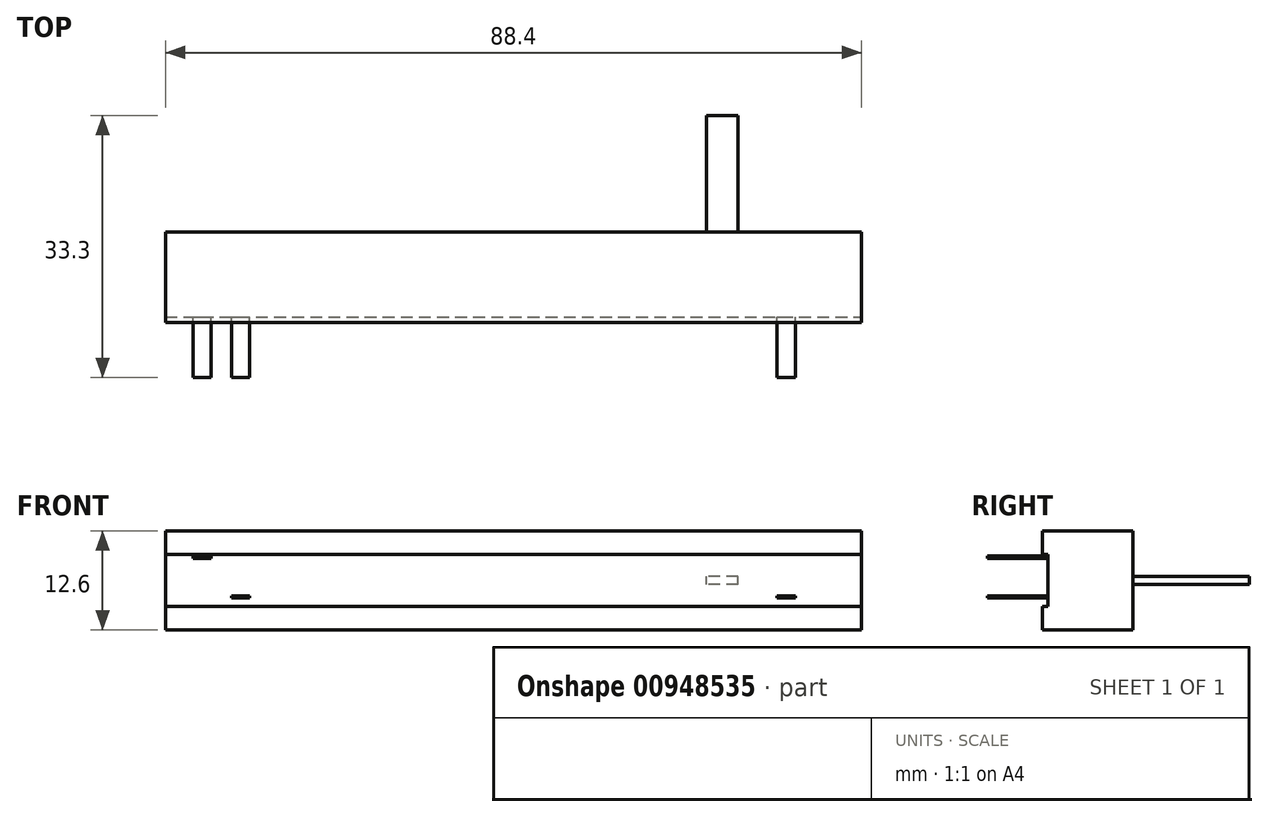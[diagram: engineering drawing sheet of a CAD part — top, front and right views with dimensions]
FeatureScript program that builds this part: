
annotation { "Feature Type Name" : "Feature", "Feature Type Description" : "" }
export const myFeature = defineFeature(function(context is Context, id is Id, definition is map)
    precondition{}
    {
        {
            var Q0;
            Q0=qCreatedBy(makeId("Front.planeOp"),FACE);
            var sketch = newSketch(context, id + "F0", { "sketchPlane" : qUnion([Q0])});
            skLineSegment(sketch, "E0.bottom", {"start": v(44.2, 6.3) * mm, "end": v(-44.2, 6.3) * mm});
            skLineSegment(sketch, "E0.top", {"start": v(44.2, -6.3) * mm, "end": v(-44.2, -6.3) * mm});
            skLineSegment(sketch, "E0.left", {"start": v(44.2, 6.3) * mm, "end": v(44.2, -6.3) * mm});
            skLineSegment(sketch, "E0.right", {"start": v(-44.2, 6.3) * mm, "end": v(-44.2, -6.3) * mm});
            skPoint(sketch, "E0.middle", {"position": v(0, 0) * mm});
            skLineSegment(sketch, "E1.bottom", {"start": v(-40.7, 2.82) * mm, "end": v(-38.4, 2.82) * mm});
            skLineSegment(sketch, "E1.top", {"start": v(-40.7, 3.1) * mm, "end": v(-38.4, 3.1) * mm});
            skLineSegment(sketch, "E1.left", {"start": v(-40.7, 2.82) * mm, "end": v(-40.7, 3.1) * mm});
            skLineSegment(sketch, "E1.right", {"start": v(-38.4, 2.82) * mm, "end": v(-38.4, 3.1) * mm});
            skLineSegment(sketch, "E2.bottom", {"start": v(-35.8, -1.92) * mm, "end": v(-33.5, -1.92) * mm});
            skLineSegment(sketch, "E2.top", {"start": v(-35.8, -2.2) * mm, "end": v(-33.5, -2.2) * mm});
            skLineSegment(sketch, "E2.left", {"start": v(-35.8, -1.92) * mm, "end": v(-35.8, -2.2) * mm});
            skLineSegment(sketch, "E2.right", {"start": v(-33.5, -1.92) * mm, "end": v(-33.5, -2.2) * mm});
            skLineSegment(sketch, "E3.bottom", {"start": v(33.5, -1.92) * mm, "end": v(35.8, -1.92) * mm});
            skLineSegment(sketch, "E3.top", {"start": v(33.5, -2.2) * mm, "end": v(35.8, -2.2) * mm});
            skLineSegment(sketch, "E3.left", {"start": v(33.5, -1.92) * mm, "end": v(33.5, -2.2) * mm});
            skLineSegment(sketch, "E3.right", {"start": v(35.8, -1.92) * mm, "end": v(35.8, -2.2) * mm});
            skLineSegment(sketch, "E4.bottom", {"start": v(-44.2, -6.3) * mm, "end": v(44.2, -6.3) * mm});
            skLineSegment(sketch, "E4.top", {"start": v(-44.2, -3.3) * mm, "end": v(44.2, -3.3) * mm});
            skLineSegment(sketch, "E4.left", {"start": v(-44.2, -6.3) * mm, "end": v(-44.2, -3.3) * mm});
            skLineSegment(sketch, "E4.right", {"start": v(44.2, -6.3) * mm, "end": v(44.2, -3.3) * mm});
            skLineSegment(sketch, "E5.bottom", {"start": v(-44.2, 6.3) * mm, "end": v(44.2, 6.3) * mm});
            skLineSegment(sketch, "E5.top", {"start": v(-44.2, 3.3) * mm, "end": v(44.2, 3.3) * mm});
            skLineSegment(sketch, "E5.left", {"start": v(-44.2, 6.3) * mm, "end": v(-44.2, 3.3) * mm});
            skLineSegment(sketch, "E5.right", {"start": v(44.2, 6.3) * mm, "end": v(44.2, 3.3) * mm});
            skSolve(sketch);
        }
        {
            var Q0;
            Q0=makeQuery(id+"F0.imprint","IMPRINT",FACE,{"disambiguationData":[TD([[makeQuery(id+"F0.imprint","IMPRINT",EDGE,{"derivedFrom":sQuery(id+"F0.wireOp",EDGE,"E0.bottom")}),1.0]])]});
            var Q1;
            Q1=makeQuery(id+"F0.imprint","IMPRINT",FACE,{"disambiguationData":[TD([[makeQuery(id+"F0.imprint","IMPRINT",EDGE,{"derivedFrom":sQuery(id+"F0.wireOp",EDGE,"E1.bottom")}),1.0]])]});
            var Q2;
            Q2=makeQuery(id+"F0.imprint","IMPRINT",FACE,{"disambiguationData":[TD([[makeQuery(id+"F0.imprint","IMPRINT",EDGE,{"derivedFrom":sQuery(id+"F0.wireOp",EDGE,"E2.bottom")}),-1.0]])]});
            var Q3;
            Q3=makeQuery(id+"F0.imprint","IMPRINT",FACE,{"disambiguationData":[TD([[makeQuery(id+"F0.imprint","IMPRINT",EDGE,{"derivedFrom":sQuery(id+"F0.wireOp",EDGE,"E3.bottom")}),-1.0]])]});
            var Q4;
            Q4=makeQuery(id+"F0.imprint","IMPRINT",FACE,{"disambiguationData":[TD([[makeQuery(id+"F0.imprint","IMPRINT",EDGE,{"derivedFrom":sQuery(id+"F0.wireOp",EDGE,"E1.bottom")}),-1.0]])]});
            var Q5;
            {var subQ0=sQuery(id+"F0.wireOp",EDGE,"E0.top");Q5=makeQuery(id+"F0.imprint","IMPRINT",FACE,{"disambiguationData":[TD([[makeQuery(id+"F0.imprint","IMPRINT",EDGE,{"derivedFrom":subQ0}),-1.0]])]});}
            extrude(context, id + "F1", {"entities" : qUnion([Q0, Q1, Q2, Q3, Q4, Q5]), "oppositeDirection" : true, "depth" : 10.8 * mm, "offsetDistance" : 25 * mm});
        }
        {
            var Q0;
            Q0=makeQuery(id+"F0.imprint","IMPRINT",FACE,{"disambiguationData":[TD([[makeQuery(id+"F0.imprint","IMPRINT",EDGE,{"derivedFrom":sQuery(id+"F0.wireOp",EDGE,"E3.bottom")}),-1.0]])]});
            var Q1;
            Q1=makeQuery(id+"F0.imprint","IMPRINT",FACE,{"disambiguationData":[TD([[makeQuery(id+"F0.imprint","IMPRINT",EDGE,{"derivedFrom":sQuery(id+"F0.wireOp",EDGE,"E1.bottom")}),1.0]])]});
            var Q2;
            Q2=makeQuery(id+"F0.imprint","IMPRINT",FACE,{"disambiguationData":[TD([[makeQuery(id+"F0.imprint","IMPRINT",EDGE,{"derivedFrom":sQuery(id+"F0.wireOp",EDGE,"E2.bottom")}),-1.0]])]});
            extrude(context, id + "F2", {"entities" : qUnion([Q0, Q1, Q2]), "operationType" : NewBodyOperationType.ADD, "depth" : 7.7 * mm, "offsetDistance" : 25 * mm});
        }
        {
            var Q0;
            {var subQ0=sQuery(id+"F0.wireOp",EDGE,"E0.bottom");Q0=makeQuery(id+"F0.imprint","IMPRINT",FACE,{"disambiguationData":[TD([[makeQuery(id+"F0.imprint","IMPRINT",EDGE,{"derivedFrom":subQ0}),1.0]])]});}
            var Q1;
            {var subQ0=sQuery(id+"F0.wireOp",EDGE,"E0.top");Q1=makeQuery(id+"F0.imprint","IMPRINT",FACE,{"disambiguationData":[TD([[makeQuery(id+"F0.imprint","IMPRINT",EDGE,{"derivedFrom":subQ0}),-1.0]])]});}
            extrude(context, id + "F3", {"entities" : qUnion([Q0, Q1]), "operationType" : NewBodyOperationType.ADD, "depth" : 11.5 * mm - 10.8 * mm, "offsetDistance" : 25 * mm});
        }
        {
            var Q0;
            Q0=makeQuery(id+"F1.opExtrude","CAP_FACE",FACE,{"disambiguationData":[OSD([sQuery(id+"F0.wireOp",EDGE,"E0.bottom"),sQuery(id+"F0.wireOp",EDGE,"E0.top"),sQuery(id+"F0.wireOp",EDGE,"E0.left"),sQuery(id+"F0.wireOp",EDGE,"E0.right")])],"isStart":false});
            var sketch = newSketch(context, id + "F4", { "sketchPlane" : qUnion([Q0])});
            skLineSegment(sketch, "E6.bottom", {"start": v(-28.55, -0.5) * mm, "end": v(-24.55, -0.5) * mm});
            skLineSegment(sketch, "E6.top", {"start": v(-28.55, 0.5) * mm, "end": v(-24.55, 0.5) * mm});
            skLineSegment(sketch, "E6.left", {"start": v(-28.55, -0.5) * mm, "end": v(-28.55, 0.5) * mm});
            skLineSegment(sketch, "E6.right", {"start": v(-24.55, -0.5) * mm, "end": v(-24.55, 0.5) * mm});
            skPoint(sketch, "E6.middle", {"position": v(-26.55, 0) * mm});
            skSolve(sketch);
        }
        {
            var Q0;
            Q0=makeQuery(id+"F4.imprint","IMPRINT",FACE,{"disambiguationData":[TD([[makeQuery(id+"F4.imprint","IMPRINT",EDGE,{"derivedFrom":sQuery(id+"F4.wireOp",EDGE,"E6.bottom")}),1.0]])]});
            extrude(context, id + "F5", {"entities" : qUnion([Q0]), "depth" : 14.8 * mm, "offsetDistance" : 25 * mm});
        }
    });
